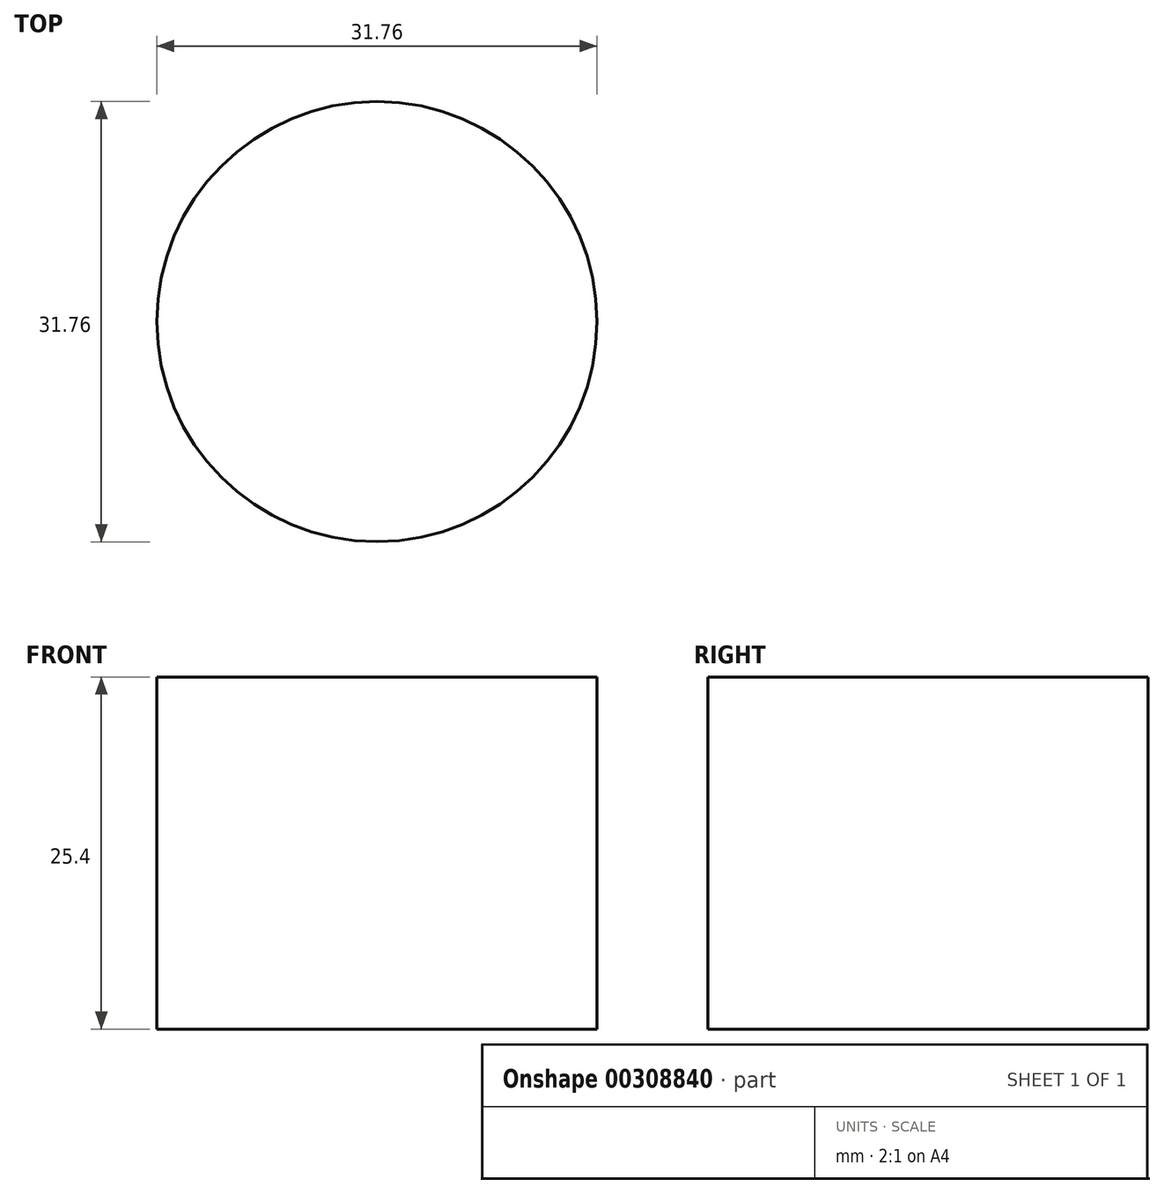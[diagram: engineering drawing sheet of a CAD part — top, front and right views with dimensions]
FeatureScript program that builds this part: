
annotation { "Feature Type Name" : "Feature", "Feature Type Description" : "" }
export const myFeature = defineFeature(function(context is Context, id is Id, definition is map)
    precondition{}
    {
        {
            var Q0;
            Q0=qCreatedBy(makeId("Top.planeOp"),FACE);
            var sketch = newSketch(context, id + "F0", { "sketchPlane" : qUnion([Q0])});
            skCircle(sketch, "E0", {"center": v(0, 0) * mm, "radius": 15.88 * mm});
            skSolve(sketch);
        }
        {
            var Q0;
            Q0=makeQuery(id+"F0.imprint","IMPRINT",FACE,{"disambiguationData":[TD([[makeQuery(id+"F0.imprint","IMPRINT",EDGE,{"derivedFrom":sQuery(id+"F0.wireOp",EDGE,"E0")}),1.0]])]});
            extrude(context, id + "F1", {"entities" : qUnion([Q0]), "depth" : 25.4 * mm});
        }
    });
